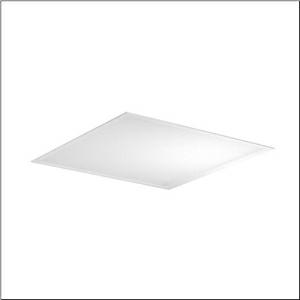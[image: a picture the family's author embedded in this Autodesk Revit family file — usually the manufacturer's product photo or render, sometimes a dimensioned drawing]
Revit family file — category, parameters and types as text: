
# Revit family: apollon_r__21_square_51mq12wd2453_b009
name_source: partatom
category: Lighting Fixtures
units: mm (PartAtom-declared; Revit-internal decimal feet)

## family parameters
Cut with Voids When Loaded = No
Host = Face
Light Source = No
Part Type = Normal
Room Calculation Point = No
Round Connector Dimension = Use Diameter
Shared = No

## types (1)
- Apollon® 21 square (1 x LED, 4000 lm, 33 W, 4000K)
    Apparent Load = 33 VA
    CIE Flux Codes = 62 88 98 100 100
    Color Rendering = 80
    Color Temperature = 4000K
    Default Elevation = 1800 mm
    Description = Apollon® 21 square, office luminaire, primary optical cover: micro prismatic cover, of PMMA, CAT 2 (L<= 3000cd/m²), light emission: direct distribution, primary light characteristic: symmetric, installation type: lay-in mounting, LED, rated luminous flux: 4.000lm, luminous efficacy: 121lm/W, light colour: 840, colour temperature: 4000K, control gear: ECG DALI, with terminal, 5-pole, mains connection: 220..240V, AC, 50/60Hz, rated input power: 33W, housing, of aluminium, traffic white (RAL 9016), module: M600, length: 596mm, width: 596mm, height: 40mm, housing upper side, of sheet steel, galvanised, protection rating (complete): IP20, protection rating (lamp compartment, on room side): IP54, insulation class (complete): insulation class II (safety insulation), certification: CE, ENEC, permissible operating ambient temperature: -20..+40°C, packaging unit: 1 piece
    Height = 0 mm  [stored 0 ft]
    Lamp = 1 x LED
    Lamp Light Flux = 4000 lm
    Lamp Power = 33 W
    Lamp count = 1
    Length = 595 mm
    Luminous efficacy = 121 lm/W
    Manufacturer = Siteco
    ModVariant = No
    Model = 51MQ12WD2453
    Mounting Place = Ceiling
    Mounting Type = Recessed
    Number of Poles = 1
    OnlyDefault = Yes
    Power Factor = 1
    Product Name = Apollon® 21 square
    Product group = office luminaire | ceiling recessed
    ProductGroupID = 400
    Protection Class = Protection class II
    Protection Degree = IP 20
    RLX_Detail_Level = 1
    RlxData = <blob elided: 14489 chars, md5=892adc31>
    Socket = socket
    Standby Power = 0 W
    System Light Flux = 4000 lm
    System Power = 33 W
    Type Comments = Product without accessories
    Type Image = l_1006118.jpg
    URL = http://relux.com
    VarID = ---
    Voltage = 0 V
    Weight = 0.00 kg
    Width = 595 mm

note: [stored X ft] marks values corroborated as IEEE doubles in the binary element streams (Revit-internal decimal feet)

## geometry (parser evidence)
native form markers: Sweep x11
no freeform markers — native parametric forms only
